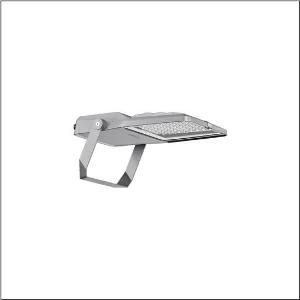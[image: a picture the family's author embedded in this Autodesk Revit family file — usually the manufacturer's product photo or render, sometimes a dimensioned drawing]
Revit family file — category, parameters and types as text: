
# Revit family: floodlight_fl_21_iq_mini___pl52_5xa7772b5d1a_4874
name_source: partatom
category: Lighting Fixtures
units: mm (PartAtom-declared; Revit-internal decimal feet)

## family parameters
Cut with Voids When Loaded = No
Host = Face
Light Source = No
Part Type = Normal
Room Calculation Point = No
Round Connector Dimension = Use Diameter
Shared = No

## types (1)
- --- (1 x LED, 5820 lm, 45.5 W, 4000K)
    Apparent Load = 46 VA
    CIE Flux Codes = 26 60 98 100 100
    Color Rendering = 80
    Color Temperature = 4000K
    Default Elevation = 1800 mm
    Description = Floodlight FL 21 iQ mini, floodlight, primary light control with lens, of PMMA, primary optical cover: protective disc, of toughened safety glass, transparent, light distribution: PL52, light emission: direct distribution, installation type: surface-mounted, LED, High Power LED, rated luminous flux: 5.820lm, luminous efficacy: 128lm/W, light colour: 840, colour temperature: 4000K, control: Street-Remote, Auto-Match, Temp-Guard, Night-Set, Smart-Wire, Desk-Remote (wireless, voltage-free reading and setting of iQ features in the workshop via application-optimized NFC function/RFID function), optimised constant luminous flux control (CLO 2.0), with terminal, 6-pole, mains connection: 220..240V, AC, 50/60Hz, start of lifetime: 46W, end of service life: 48W, reduction: 22W, luminaire housing, of diecast aluminium, powder-coated, Siteco® metallic grey (DB 702S), corrosivity category C5 mid according to DIN EN ISO 12944, sealing non-destructively replaceable, mounting bracket, of steel, galvanised, powder-coated, Siteco® metallic grey (DB 702S), protection rating (complete): IP66, insulation class (complete): insulation class II (safety insulation), certification: CE, ENEC, VDE, protection symbol: D, impact resistance: IK08, permissible operating ambient temperature: -40..+40°C, permissible operating ambient temperature for outdoor applications: -40..+50°C, standard: DIN EN 12944, LABS conformity tested according to VDMA 24364:2018-05, packaging unit: 1 piece

Light Distribution: PL52
    Height = 70 mm
    Lamp = 1 x LED
    Lamp Light Flux = 5820 lm
    Lamp Power = 45.5 W
    Lamp count = 1
    Length = 485 mm
    Luminous efficacy = 128 lm/W
    Manufacturer = Siteco
    ModVariant = No
    Model = 5XA7772B5D1A
    Number of Poles = 1
    OnlyDefault = Yes
    Power Factor = 1
    Product Name = Floodlight FL 21 iQ mini | PL52
    Product group = floodlight | pylon annexe
    ProductGroupID = 6200
    Protection Class = Protection class II
    Protection Degree = IP 66
    RLX_Detail_Level = 1
    RLX_Emergency_Light_Flux = 0 lm
    RLX_Emergency_Type = 0
    RLX_Emergency_Type_DB = No
    RlxData = <blob elided: 96233 chars, md5=09bd4c73>
    Socket = socket
    Standby Power = 0 W
    System Light Flux = 5820 lm
    System Power = 46 W
    Type Comments = factory setting: luminous flux: 100 % | dim-lin: 254 | 463 mA
    Type Image = l_1006845.jpg
    URL = http://relux.com
    VarID = @adj_096963
    Voltage = 0 V
    Weight = 0.00 kg
    Width = 337 mm

## geometry (parser evidence)
native form markers: Blend x4, Sweep x12
no freeform markers — native parametric forms only
